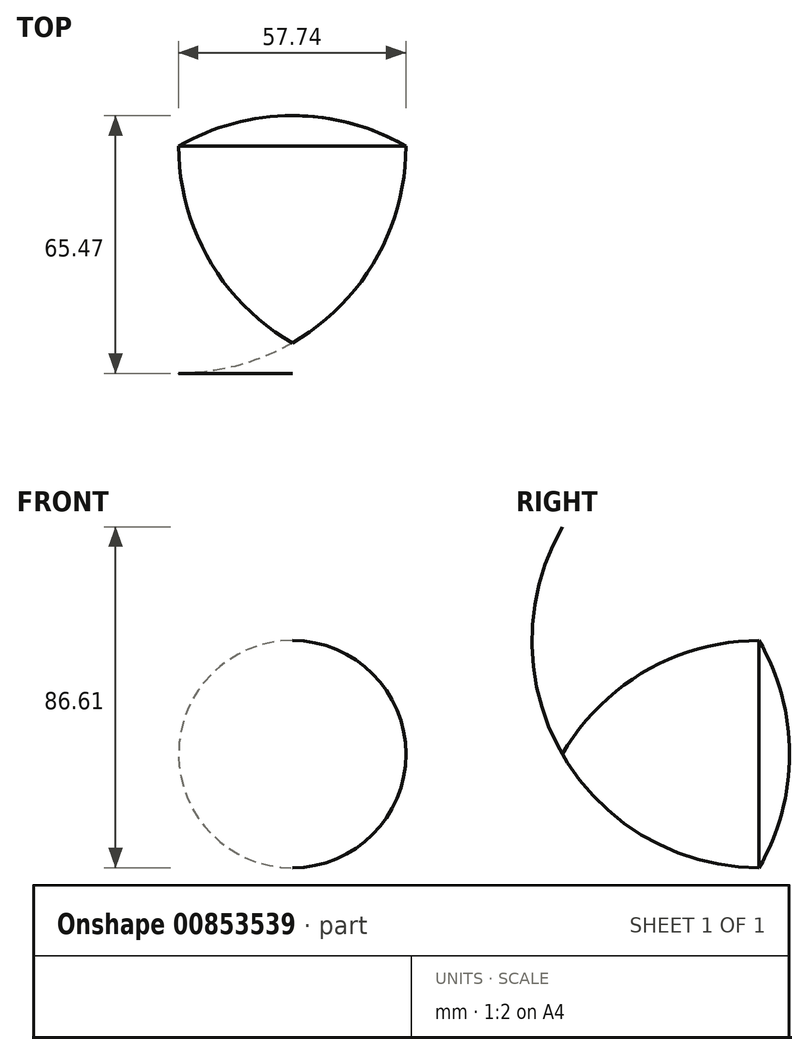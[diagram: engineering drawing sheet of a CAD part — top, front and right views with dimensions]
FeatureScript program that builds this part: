
annotation { "Feature Type Name" : "Feature", "Feature Type Description" : "" }
export const myFeature = defineFeature(function(context is Context, id is Id, definition is map)
    precondition{}
    {
        {
            var Q0;
            Q0=qCreatedBy(makeId("Top.planeOp"),FACE);
            var sketch = newSketch(context, id + "F0", { "sketchPlane" : qUnion([Q0])});
            skCircle(sketch, "E0.cCircle", {"center": v(0, 0) * mm, "radius": 16.67 * mm, "construction": true});
            skLineSegment(sketch, "E0.0", {"start": v(-28.87, 16.67) * mm, "end": v(28.87, 16.67) * mm, "construction": true});
            skLineSegment(sketch, "E0.1", {"start": v(28.87, 16.67) * mm, "end": v(0, -33.33) * mm, "construction": true});
            skLineSegment(sketch, "E0.2", {"start": v(0, -33.33) * mm, "end": v(-28.87, 16.67) * mm, "construction": true});
            skPoint(sketch, "E0.0.midPoint", {"position": v(0, 16.67) * mm});
            skArc(sketch, "E1", {"start": v(28.87, 16.67) * mm, "mid": v(0, 24.4) * mm, "end": v(-28.87, 16.67) * mm});
            skArc(sketch, "E2", {"start": v(0, -33.33) * mm, "mid": v(21.13, -12.2) * mm, "end": v(28.87, 16.67) * mm});
            skArc(sketch, "E3", {"start": v(-28.87, 16.67) * mm, "mid": v(-21.13, -12.2) * mm, "end": v(0, -33.33) * mm});
            skLineSegment(sketch, "E4", {"start": v(0, 24.4) * mm, "end": v(0, -33.33) * mm});
            skSolve(sketch);
        }
        {
            var Q0;
            {var subQ0=sQuery(id+"F0.wireOp",EDGE,"E2");Q0=makeQuery(id+"F0.imprint","IMPRINT",FACE,{"disambiguationData":[TD([[makeQuery(id+"F0.imprint","IMPRINT",EDGE,{"derivedFrom":subQ0}),1.0]])]});}
            var Q1;
            Q1=sQuery(id+"F0.wireOp",EDGE,"E4");
            revolve(context, id + "F1", {"surfaceOperationType" : NewSurfaceOperationType.NEW, "entities" : qUnion([Q0]), "axis" : qUnion([Q1]), "revolveType" : RevolveType.FULL});
        }
    });
